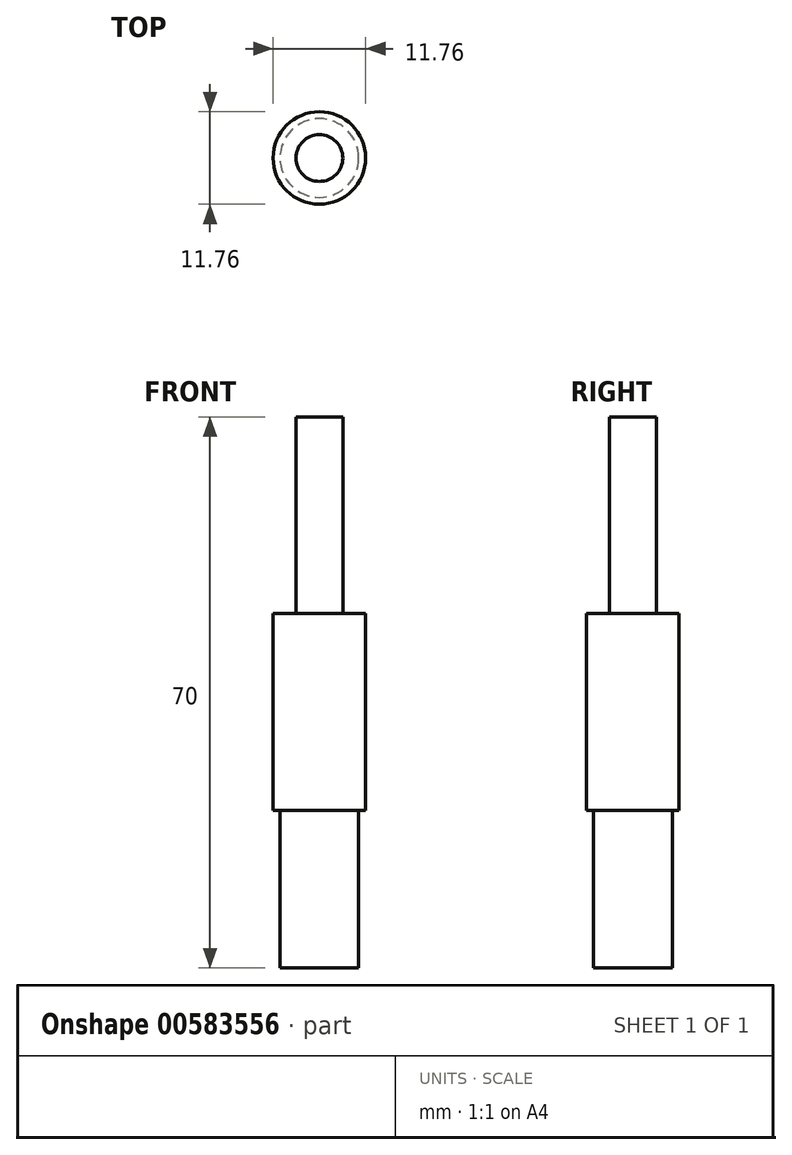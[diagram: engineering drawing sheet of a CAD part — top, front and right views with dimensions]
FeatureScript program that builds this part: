
annotation { "Feature Type Name" : "Feature", "Feature Type Description" : "" }
export const myFeature = defineFeature(function(context is Context, id is Id, definition is map)
    precondition{}
    {
        {
            var Q0;
            Q0=qCreatedBy(makeId("Top.planeOp"),FACE);
            var sketch = newSketch(context, id + "F0", { "sketchPlane" : qUnion([Q0])});
            skCircle(sketch, "E0", {"center": v(0, 0) * mm, "radius": 5.88 * mm});
            skSolve(sketch);
        }
        {
            var Q0;
            Q0 = qSketchRegion(id + "F0", true);
            extrude(context, id + "F1", {"entities" : qUnion([Q0]), "depth" : 25 * mm, "offsetDistance" : 25 * mm});
        }
        {
            var Q0;
            Q0=makeQuery(id+"F1.opExtrude","CAP_FACE",FACE,{"disambiguationData":[OSD([sQuery(id+"F0.wireOp",EDGE,"E0")])],"isStart":false});
            var sketch = newSketch(context, id + "F2", { "sketchPlane" : qUnion([Q0])});
            skCircle(sketch, "E1", {"center": v(0, 0) * mm, "radius": 2.98 * mm});
            skSolve(sketch);
        }
        {
            var Q0;
            Q0 = qSketchRegion(id + "F2", true);
            extrude(context, id + "F3", {"entities" : qUnion([Q0]), "operationType" : NewBodyOperationType.ADD, "depth" : 25 * mm, "offsetDistance" : 25 * mm});
        }
        {
            var Q0;
            Q0=makeQuery(id+"F1.opExtrude","CAP_FACE",FACE,{"disambiguationData":[OSD([sQuery(id+"F0.wireOp",EDGE,"E0")])],"isStart":true});
            var sketch = newSketch(context, id + "F4", { "sketchPlane" : qUnion([Q0])});
            skCircle(sketch, "E2", {"center": v(0, 0) * mm, "radius": 5 * mm});
            skSolve(sketch);
        }
        {
            var Q0;
            Q0 = qSketchRegion(id + "F4", true);
            extrude(context, id + "F5", {"entities" : qUnion([Q0]), "operationType" : NewBodyOperationType.ADD, "depth" : 20 * mm, "offsetDistance" : 25 * mm});
        }
    });
